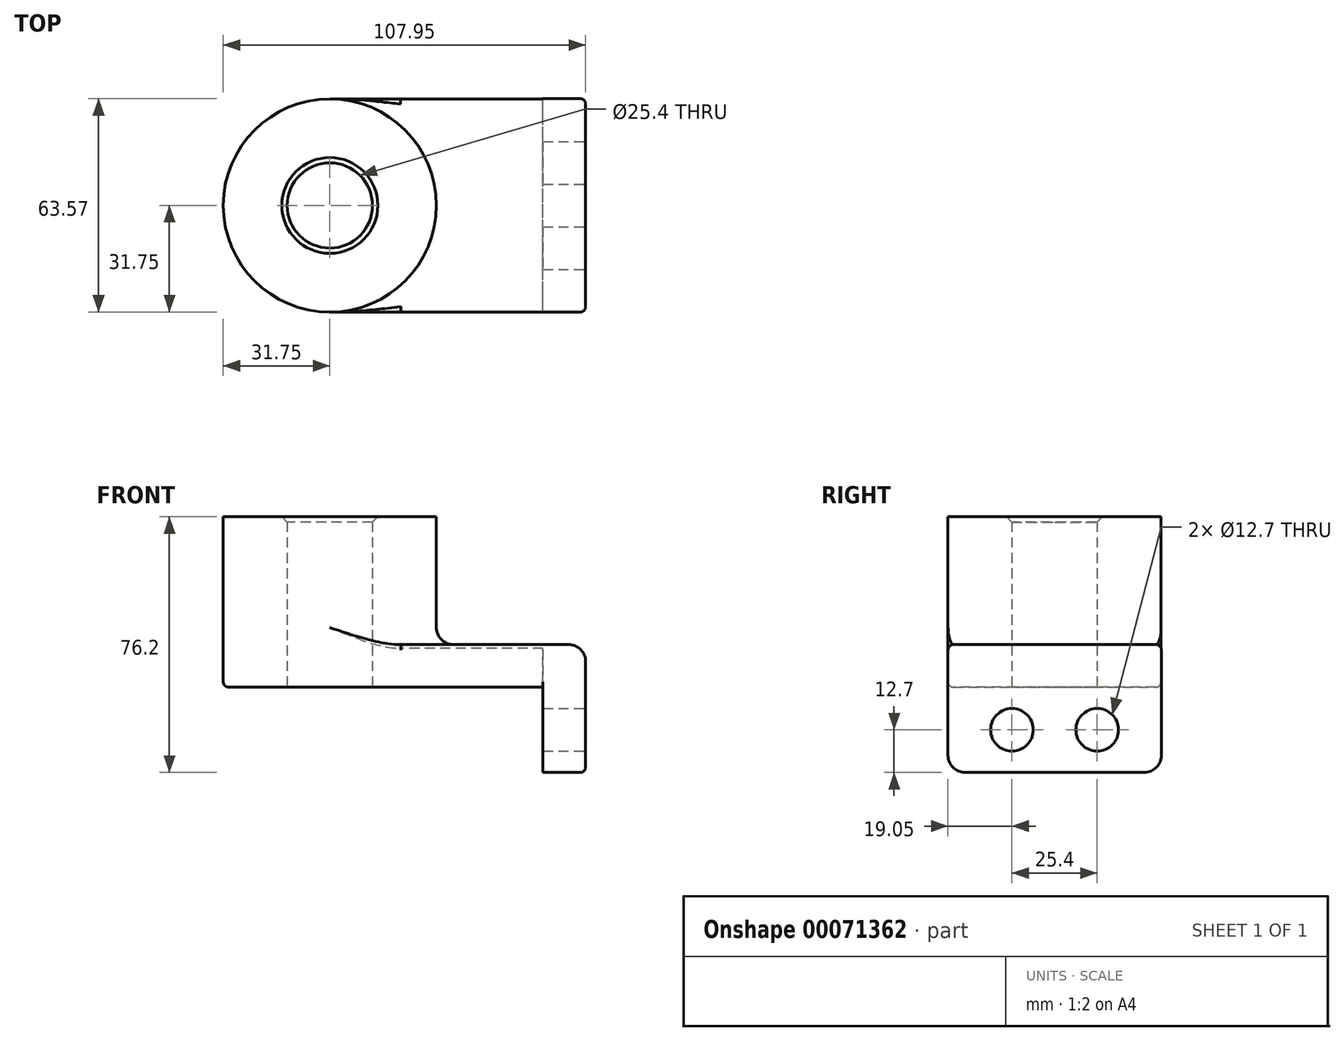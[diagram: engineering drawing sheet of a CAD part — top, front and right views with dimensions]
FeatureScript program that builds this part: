
annotation { "Feature Type Name" : "Feature", "Feature Type Description" : "" }
export const myFeature = defineFeature(function(context is Context, id is Id, definition is map)
    precondition{}
    {
        {
            var Q0;
            Q0=qCreatedBy(makeId("Top.planeOp"),FACE);
            var sketch = newSketch(context, id + "F0", { "sketchPlane" : qUnion([Q0])});
            skLineSegment(sketch, "E0.rect.bottom", {"start": v(38.1, -31.75) * mm, "end": v(-38.1, -31.75) * mm});
            skLineSegment(sketch, "E0.rect.top", {"start": v(38.1, 31.75) * mm, "end": v(-38.1, 31.75) * mm});
            skLineSegment(sketch, "E0.rect.left", {"start": v(38.1, -31.75) * mm, "end": v(38.1, 31.75) * mm});
            skLineSegment(sketch, "E0.rect.right", {"start": v(-38.1, -31.75) * mm, "end": v(-38.1, 31.75) * mm});
            skPoint(sketch, "E0.rect.middle", {"position": v(0, 0) * mm});
            skCircle(sketch, "E1", {"center": v(-38.1, 0) * mm, "radius": 31.75 * mm});
            skCircle(sketch, "E2", {"center": v(-38.1, 0) * mm, "radius": 12.7 * mm});
            skSolve(sketch);
        }
        {
            var Q0;
            Q0 = qSketchRegion(id + "F0", true);
            extrude(context, id + "F1", {"entities" : qUnion([Q0]), "depth" : 12.7 * mm});
        }
        {
            var Q0;
            {var subQ1=sQuery(id+"F0.wireOp",EDGE,"E0.rect.right");var subQ3=sQuery(id+"F0.wireOp",EDGE,"E2");var subQ4=makeQuery(id+"F0.imprint","INTERSECT",VERTEX,{"disambiguationData":[OD(0.0)],"derivedFrom":[subQ1,subQ3]});Q0=makeQuery(id+"F0.imprint","IMPRINT",FACE,{"disambiguationData":[TD([[makeQuery(id+"F0.imprint","IMPRINT",EDGE,{"disambiguationData":[TD([[subQ4,-1.0]])],"derivedFrom":subQ3}),-1.0]])]});}
            var Q1;
            {var subQ1=sQuery(id+"F0.wireOp",EDGE,"E0.rect.right");var subQ3=sQuery(id+"F0.wireOp",EDGE,"E2");var subQ4=makeQuery(id+"F0.imprint","INTERSECT",VERTEX,{"disambiguationData":[OD(0.0)],"derivedFrom":[subQ1,subQ3]});Q1=makeQuery(id+"F0.imprint","IMPRINT",FACE,{"disambiguationData":[TD([[makeQuery(id+"F0.imprint","IMPRINT",EDGE,{"disambiguationData":[TD([[subQ4,1.0]])],"derivedFrom":subQ3}),-1.0]])]});}
            extrude(context, id + "F2", {"entities" : qUnion([Q0, Q1]), "operationType" : NewBodyOperationType.ADD, "depth" : 50.8 * mm});
        }
        {
            var Q0;
            Q0=makeQuery(id+"F1.opExtrude","SWEPT_FACE",FACE,{"disambiguationData":[OSD([sQuery(id+"F0.wireOp",EDGE,"E0.rect.left")])]});
            var sketch = newSketch(context, id + "F3", { "sketchPlane" : qUnion([Q0])});
            skLineSegment(sketch, "E3.bottom", {"start": v(-31.75, 12.7) * mm, "end": v(31.82, 12.7) * mm});
            skLineSegment(sketch, "E3.top", {"start": v(-31.75, -25.4) * mm, "end": v(31.82, -25.4) * mm});
            skLineSegment(sketch, "E3.left", {"start": v(-31.75, 12.7) * mm, "end": v(-31.75, -25.4) * mm});
            skLineSegment(sketch, "E3.right", {"start": v(31.82, 12.7) * mm, "end": v(31.82, -25.4) * mm});
            skCircle(sketch, "E4", {"center": v(-12.7, -12.7) * mm, "radius": 6.35 * mm});
            skLineSegment(sketch, "E5", {"start": v(0, 0) * mm, "end": v(0, -25.4) * mm, "construction": true});
            skCircle(sketch, "E6.MirrorC", {"center": v(12.7, -12.7) * mm, "radius": 6.35 * mm});
            skSolve(sketch);
        }
        {
            var Q0;
            Q0 = qSketchRegion(id + "F3", true);
            extrude(context, id + "F4", {"entities" : qUnion([Q0]), "operationType" : NewBodyOperationType.ADD, "oppositeDirection" : true, "depth" : 12.7 * mm});
        }
        {
            var Q0;
            {var subQ0=sQuery(id+"F0.wireOp",EDGE,"E1");Q0=makeQuery(id+"F2.boolean.opBoolean","INTERSECT",EDGE,{"derivedFrom":[makeQuery(id+"F1.opExtrude","CAP_FACE",FACE,{"disambiguationData":[OSD([sQuery(id+"F0.wireOp",EDGE,"E0.rect.bottom"),sQuery(id+"F0.wireOp",EDGE,"E0.rect.top"),sQuery(id+"F0.wireOp",EDGE,"E0.rect.left"),subQ0,sQuery(id+"F0.wireOp",EDGE,"E2")])],"isStart":false}),makeQuery(id+"F2.opExtrude","SWEPT_FACE",FACE,{"disambiguationData":[OSD([subQ0])]})]});}
            var Q1;
            Q1=makeQuery(id+"F4.boolean.opBoolean","MERGE",EDGE,{"derivedFrom":[makeQuery(id+"F1.opExtrude","CAP_EDGE",EDGE,{"disambiguationData":[OSD([sQuery(id+"F0.wireOp",EDGE,"E0.rect.left")])],"isStart":false}),makeQuery(id+"F4.opExtrude","CAP_EDGE",EDGE,{"disambiguationData":[OSD([sQuery(id+"F3.wireOp",EDGE,"E3.bottom")])],"isStart":true})]});
            var Q2;
            Q2=makeQuery(id+"F4.opExtrude","SWEPT_EDGE",EDGE,{"disambiguationData":[OSD([sQuery(id+"F3.wireOp",EDGE,"E3.top"),sQuery(id+"F3.wireOp",EDGE,"E3.left")])]});
            var Q3;
            Q3=makeQuery(id+"F4.opExtrude","SWEPT_EDGE",EDGE,{"disambiguationData":[OSD([sQuery(id+"F3.wireOp",EDGE,"E3.top"),sQuery(id+"F3.wireOp",EDGE,"E3.right")])]});
            fillet(context, id + "F5", {"entities" : qUnion([Q0, Q1, Q2, Q3]), "radius" : 5.08 * mm, "tangentPropagation" : true, "allowEdgeOverflow" : false});
        }
        {
            var Q0;
            Q0=makeQuery(id+"F2.opExtrude","CAP_EDGE",EDGE,{"disambiguationData":[OSD([sQuery(id+"F0.wireOp",EDGE,"E2")])],"isStart":false});
            chamfer(context, id + "F6", {"entities" : qUnion([Q0]), "width" : 1.59 * mm, "tangentPropagation" : true});
        }
        {
            var Q0;
            Q0=makeQuery(id+"F1.opExtrude","CAP_EDGE",EDGE,{"disambiguationData":[OSD([sQuery(id+"F0.wireOp",EDGE,"E0.rect.bottom")])],"isStart":false});
            var Q1;
            Q1=makeQuery(id+"F1.opExtrude","CAP_EDGE",EDGE,{"disambiguationData":[OSD([sQuery(id+"F0.wireOp",EDGE,"E0.rect.bottom")])],"isStart":true});
            fillet(context, id + "F7", {"entities" : qUnion([Q0, Q1]), "radius" : 1.59 * mm, "tangentPropagation" : true, "allowEdgeOverflow" : false});
        }
    });
